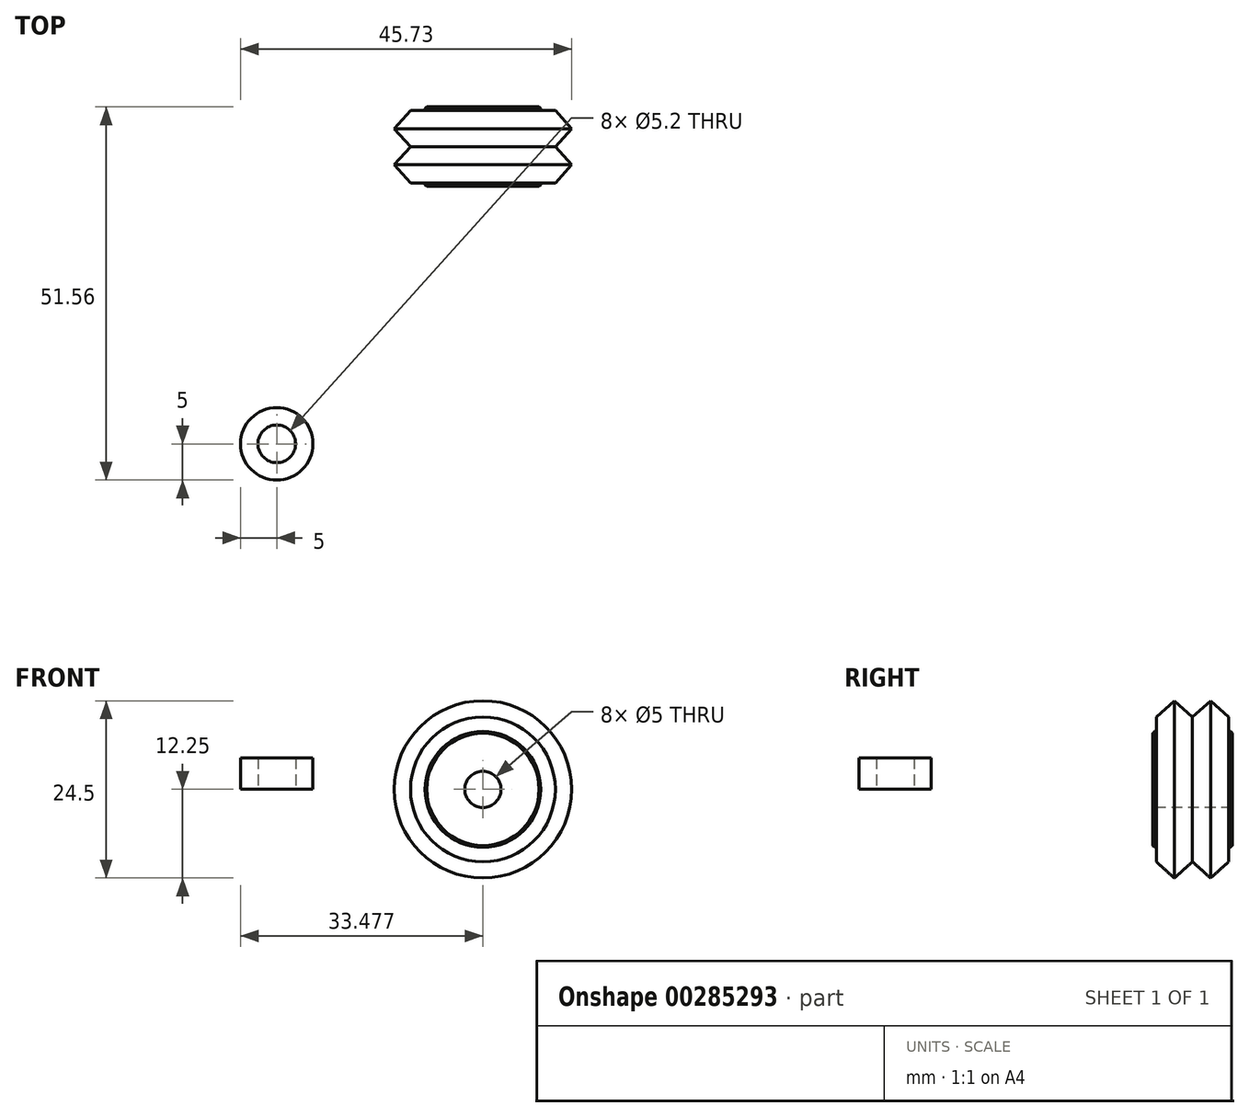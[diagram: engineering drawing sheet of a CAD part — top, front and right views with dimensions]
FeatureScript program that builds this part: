
annotation { "Feature Type Name" : "Feature", "Feature Type Description" : "" }
export const myFeature = defineFeature(function(context is Context, id is Id, definition is map)
    precondition{}
    {
        {
            var Q0;
            Q0=qCreatedBy(makeId("Top.planeOp"),FACE);
            var sketch = newSketch(context, id + "F0", { "sketchPlane" : qUnion([Q0])});
            skCircle(sketch, "E0", {"center": v(0, 0) * mm, "radius": 5 * mm});
            skCircle(sketch, "E1", {"center": v(0, 0) * mm, "radius": 2.6 * mm});
            skSolve(sketch);
        }
        {
            var Q0;
            Q0 = qSketchRegion(id + "F0", true);
            extrude(context, id + "F1", {"entities" : qUnion([Q0]), "depth" : 4.35 * mm, "offsetDistance" : 25 * mm});
        }
        {
            var Q0;
            Q0=qCreatedBy(makeId("Top.planeOp"),FACE);
            var sketch = newSketch(context, id + "F2", { "sketchPlane" : qUnion([Q0])});
            skLineSegment(sketch, "E2", {"start": v(28.48, 34.75) * mm, "end": v(28.48, 45.75) * mm});
            skLineSegment(sketch, "E3", {"start": v(30.98, 46.56) * mm, "end": v(30.98, 35.56) * mm});
            skLineSegment(sketch, "E4", {"start": v(36.48, 46.56) * mm, "end": v(36.48, 35.56) * mm});
            skLineSegment(sketch, "E5", {"start": v(30.98, 46.56) * mm, "end": v(36.48, 46.56) * mm});
            skLineSegment(sketch, "E6", {"start": v(36.48, 35.56) * mm, "end": v(30.98, 35.56) * mm});
            skLineSegment(sketch, "E7", {"start": v(36.48, 36.06) * mm, "end": v(38.48, 36.06) * mm});
            skLineSegment(sketch, "E8", {"start": v(38.48, 36.06) * mm, "end": v(38.48, 46.06) * mm});
            skLineSegment(sketch, "E9", {"start": v(38.48, 46.06) * mm, "end": v(36.48, 46.06) * mm});
            skLineSegment(sketch, "E10", {"start": v(38.48, 36.06) * mm, "end": v(40.73, 38.56) * mm});
            skLineSegment(sketch, "E11", {"start": v(40.73, 38.56) * mm, "end": v(38.48, 41.06) * mm});
            skLineSegment(sketch, "E12", {"start": v(38.48, 41.06) * mm, "end": v(40.73, 43.56) * mm});
            skLineSegment(sketch, "E13", {"start": v(40.73, 43.56) * mm, "end": v(38.48, 46.06) * mm});
            skSolve(sketch);
        }
        {
            var Q0;
            Q0 = qSketchRegion(id + "F2", true);
            var Q1;
            Q1=sQuery(id+"F2.wireOp",EDGE,"E2");
            revolve(context, id + "F3", {"entities" : qUnion([Q0]), "axis" : qUnion([Q1]), "revolveType" : RevolveType.FULL});
        }
        {
            var Q0;
            Q0=makeQuery(id+"F3.opRevolve","SWEPT_EDGE",EDGE,{"disambiguationData":[OSD([sQuery(id+"F2.wireOp",EDGE,"E4"),sQuery(id+"F2.wireOp",EDGE,"E6")])]});
            chamfer(context, id + "F4", {"entities" : qUnion([Q0]), "width" : 0.25 * mm, "tangentPropagation" : true});
        }
        {
            var Q0;
            Q0=makeQuery(id+"F3.opRevolve","SWEPT_EDGE",EDGE,{"disambiguationData":[OSD([sQuery(id+"F2.wireOp",EDGE,"E4"),sQuery(id+"F2.wireOp",EDGE,"E5")])]});
            chamfer(context, id + "F5", {"entities" : qUnion([Q0]), "width" : 0.25 * mm, "tangentPropagation" : true});
        }
    });
